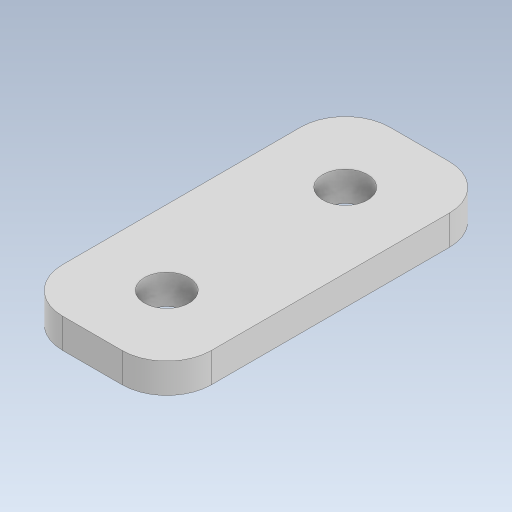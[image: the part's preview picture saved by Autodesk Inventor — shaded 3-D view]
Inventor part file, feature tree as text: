
AUTODESK INVENTOR PART (.ipt)
format: ipt  version: 2023.5 (Build 275446000, 446)  size: 275,456 bytes
history: native  units: in
note: dims shown in document units (in); Inventor stores cm internally (conversion verified against a paired STEP export)
features: extrude x1, sketch x1
ambient origin geometry x8: Origin, YZ Plane, XZ Plane, XY Plane, X Axis, Y Axis, Z Axis, Center Point
bodies: Solid1 (feature_tree)
feature tree (2):
  extrude  "Extrusion1"  Depth=0.2362in
  sketch  "Sketch1"  dims[d0=0.1181in d1=0.2362in d2=0.1969in d3=0.1969in d4=0.1181in d5=0.0787in d6=0.0in]
